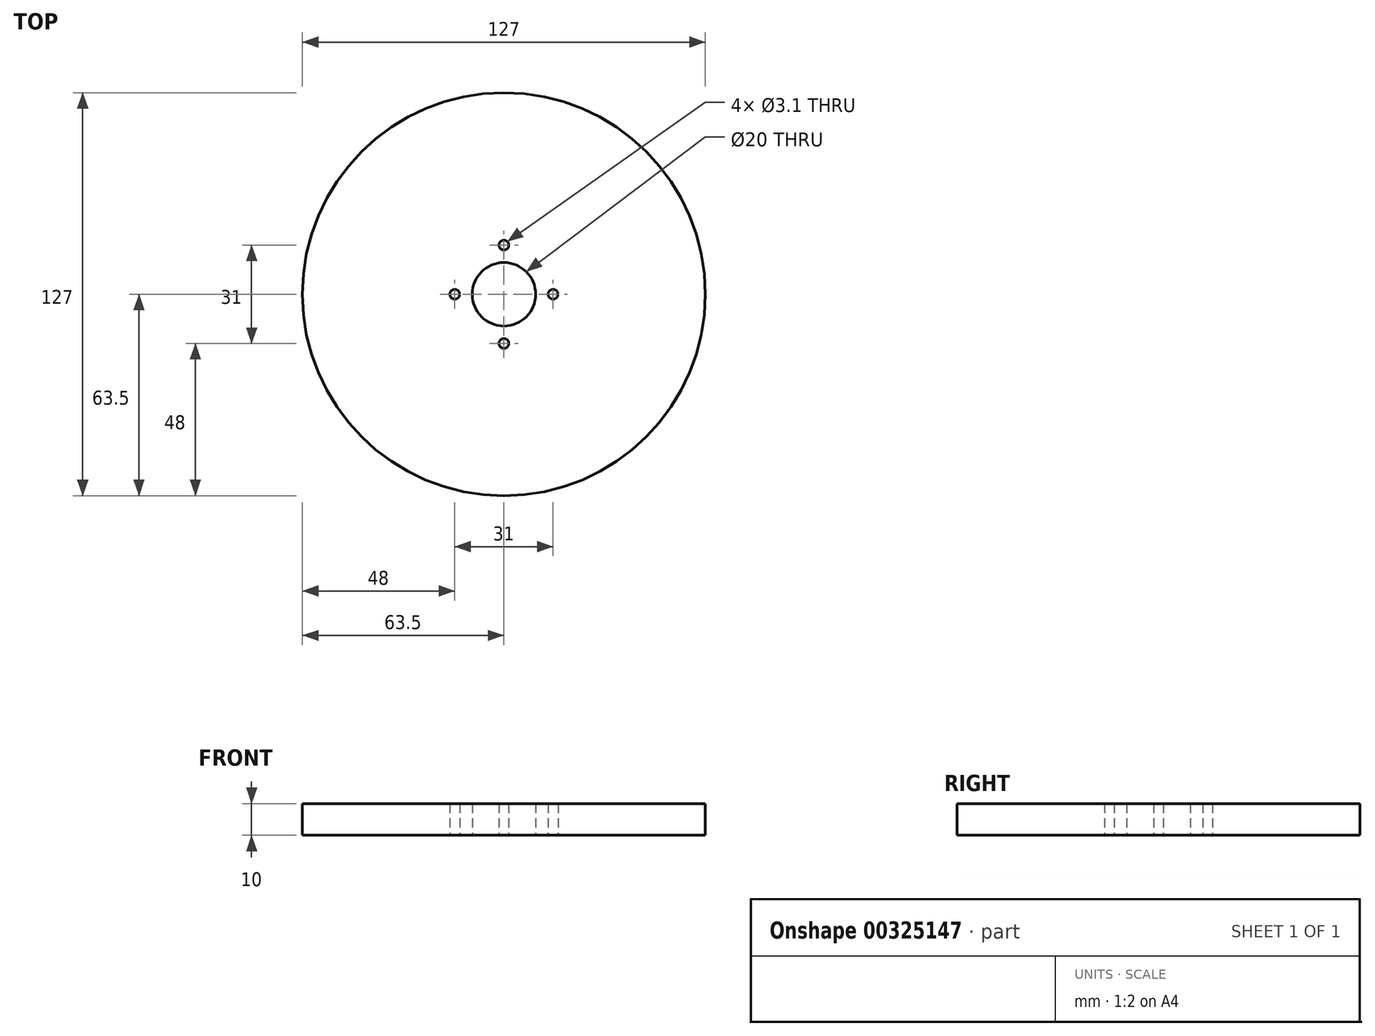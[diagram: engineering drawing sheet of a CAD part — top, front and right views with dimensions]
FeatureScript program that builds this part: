
annotation { "Feature Type Name" : "Feature", "Feature Type Description" : "" }
export const myFeature = defineFeature(function(context is Context, id is Id, definition is map)
    precondition{}
    {
        {
            var Q0;
            Q0=qCreatedBy(makeId("Top.planeOp"),FACE);
            var sketch = newSketch(context, id + "F0", { "sketchPlane" : qUnion([Q0])});
            skCircle(sketch, "E0", {"center": v(0, 0) * mm, "radius": 63.5 * mm});
            skCircle(sketch, "E1", {"center": v(0, 0) * mm, "radius": 10 * mm});
            skCircle(sketch, "E2", {"center": v(0, 0) * mm, "radius": 15.5 * mm});
            skCircle(sketch, "E3", {"center": v(-15.5, 0) * mm, "radius": 1.55 * mm});
            skCircle(sketch, "E4", {"center": v(15.5, 0) * mm, "radius": 1.55 * mm});
            skCircle(sketch, "E5", {"center": v(0, 15.5) * mm, "radius": 1.55 * mm});
            skCircle(sketch, "E6", {"center": v(0, -15.5) * mm, "radius": 1.55 * mm});
            skSolve(sketch);
        }
        {
            var Q0;
            Q0=makeQuery(id+"F0.imprint","IMPRINT",FACE,{"disambiguationData":[TD([[makeQuery(id+"F0.imprint","IMPRINT",EDGE,{"derivedFrom":sQuery(id+"F0.wireOp",EDGE,"E0")}),1.0]])]});
            var Q1;
            Q1=makeQuery(id+"F0.imprint","IMPRINT",FACE,{"disambiguationData":[TD([[makeQuery(id+"F0.imprint","IMPRINT",EDGE,{"derivedFrom":sQuery(id+"F0.wireOp",EDGE,"E1")}),-1.0]])]});
            extrude(context, id + "F1", {"entities" : qUnion([Q0, Q1]), "depth" : 10 * mm});
        }
    });
